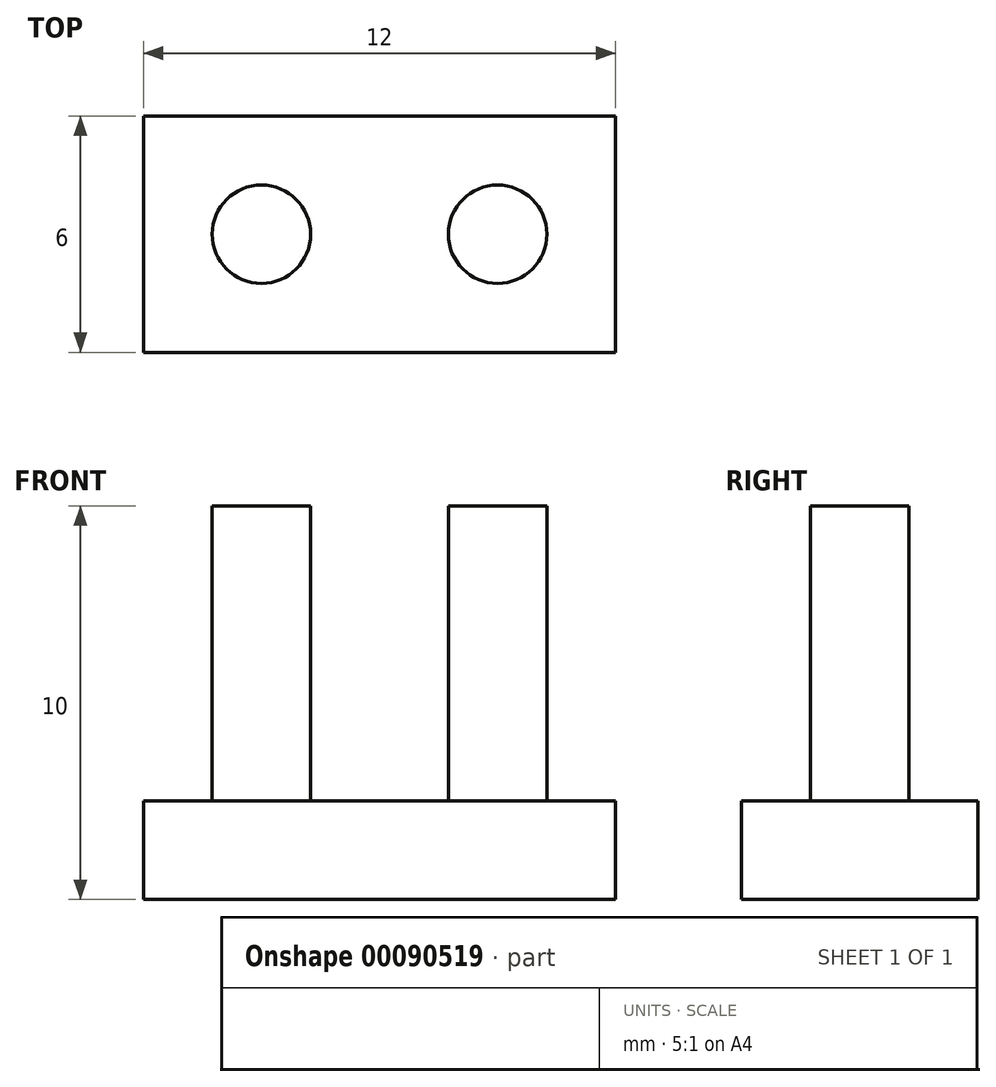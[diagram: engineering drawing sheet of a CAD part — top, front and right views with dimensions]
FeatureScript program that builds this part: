
annotation { "Feature Type Name" : "Feature", "Feature Type Description" : "" }
export const myFeature = defineFeature(function(context is Context, id is Id, definition is map)
    precondition{}
    {
        {
            var Q0;
            Q0=qCreatedBy(makeId("Top.planeOp"),FACE);
            var sketch = newSketch(context, id + "F0", { "sketchPlane" : qUnion([Q0])});
            skCircle(sketch, "E0", {"center": v(-3, 0) * mm, "radius": 2.5 * mm, "construction": true});
            skLineSegment(sketch, "E1", {"start": v(-3, 0) * mm, "end": v(0, 0) * mm, "construction": true});
            skLineSegment(sketch, "E2", {"start": v(-3, 0) * mm, "end": v(-6, 0) * mm, "construction": true});
            skLineSegment(sketch, "E3", {"start": v(-6, 0) * mm, "end": v(-9, 0) * mm, "construction": true});
            skLineSegment(sketch, "E4", {"start": v(-9, 0) * mm, "end": v(-12, 0) * mm, "construction": true});
            skCircle(sketch, "E5", {"center": v(-9, 0) * mm, "radius": 2.5 * mm, "construction": true});
            skCircle(sketch, "E6", {"center": v(-9, 0) * mm, "radius": 1.25 * mm});
            skCircle(sketch, "E7", {"center": v(-3, 0) * mm, "radius": 1.25 * mm});
            skLineSegment(sketch, "E8.bottom", {"start": v(0, 0) * mm, "end": v(-12, 0) * mm});
            skLineSegment(sketch, "E8.top", {"start": v(0, 3) * mm, "end": v(-12, 3) * mm});
            skLineSegment(sketch, "E8.left", {"start": v(0, 0) * mm, "end": v(0, 3) * mm});
            skLineSegment(sketch, "E8.right", {"start": v(-12, 0) * mm, "end": v(-12, 3) * mm});
            skLineSegment(sketch, "E9.top", {"start": v(0, -3) * mm, "end": v(-12, -3) * mm});
            skLineSegment(sketch, "E9.left", {"start": v(0, 0) * mm, "end": v(0, -3) * mm});
            skLineSegment(sketch, "E9.right", {"start": v(-12, 0) * mm, "end": v(-12, -3) * mm});
            skSolve(sketch);
        }
        {
            var Q0;
            Q0 = qSketchRegion(id + "F0", true);
            var Q1;
            {var subQ0=sQuery(id+"F0.wireOp",EDGE,"E8.bottom");var subQ1=sQuery(id+"F0.wireOp",EDGE,"E6");var subQ2=makeQuery(id+"F0.imprint","INTERSECT",VERTEX,{"disambiguationData":[OD(0.0)],"derivedFrom":[subQ1,subQ0]});Q1=makeQuery(id+"F0.imprint","IMPRINT",FACE,{"disambiguationData":[TD([[makeQuery(id+"F0.imprint","IMPRINT",EDGE,{"disambiguationData":[TD([[subQ2,1.0]])],"derivedFrom":subQ1}),1.0]])]});}
            var Q2;
            {var subQ0=sQuery(id+"F0.wireOp",EDGE,"E8.bottom");var subQ1=sQuery(id+"F0.wireOp",EDGE,"E6");var subQ2=makeQuery(id+"F0.imprint","INTERSECT",VERTEX,{"disambiguationData":[OD(0.0)],"derivedFrom":[subQ1,subQ0]});Q2=makeQuery(id+"F0.imprint","IMPRINT",FACE,{"disambiguationData":[TD([[makeQuery(id+"F0.imprint","IMPRINT",EDGE,{"disambiguationData":[TD([[subQ2,-1.0]])],"derivedFrom":subQ1}),1.0]])]});}
            var Q3;
            {var subQ0=sQuery(id+"F0.wireOp",EDGE,"E8.bottom");var subQ1=sQuery(id+"F0.wireOp",EDGE,"E7");var subQ2=makeQuery(id+"F0.imprint","INTERSECT",VERTEX,{"disambiguationData":[OD(0.0)],"derivedFrom":[subQ1,subQ0]});Q3=makeQuery(id+"F0.imprint","IMPRINT",FACE,{"disambiguationData":[TD([[makeQuery(id+"F0.imprint","IMPRINT",EDGE,{"disambiguationData":[TD([[subQ2,1.0]])],"derivedFrom":subQ1}),1.0]])]});}
            var Q4;
            {var subQ0=sQuery(id+"F0.wireOp",EDGE,"E8.bottom");var subQ1=sQuery(id+"F0.wireOp",EDGE,"E7");var subQ2=makeQuery(id+"F0.imprint","INTERSECT",VERTEX,{"disambiguationData":[OD(0.0)],"derivedFrom":[subQ1,subQ0]});Q4=makeQuery(id+"F0.imprint","IMPRINT",FACE,{"disambiguationData":[TD([[makeQuery(id+"F0.imprint","IMPRINT",EDGE,{"disambiguationData":[TD([[subQ2,-1.0]])],"derivedFrom":subQ1}),1.0]])]});}
            extrude(context, id + "F1", {"entities" : qUnion([Q0, Q1, Q2, Q3, Q4]), "oppositeDirection" : true, "depth" : 2.5 * mm});
        }
        {
            var Q0;
            {var subQ0=sQuery(id+"F0.wireOp",EDGE,"E8.bottom");var subQ1=sQuery(id+"F0.wireOp",EDGE,"E6");var subQ2=makeQuery(id+"F0.imprint","INTERSECT",VERTEX,{"disambiguationData":[OD(0.0)],"derivedFrom":[subQ1,subQ0]});Q0=makeQuery(id+"F0.imprint","IMPRINT",FACE,{"disambiguationData":[TD([[makeQuery(id+"F0.imprint","IMPRINT",EDGE,{"disambiguationData":[TD([[subQ2,-1.0]])],"derivedFrom":subQ1}),1.0]])]});}
            var Q1;
            {var subQ0=sQuery(id+"F0.wireOp",EDGE,"E8.bottom");var subQ1=sQuery(id+"F0.wireOp",EDGE,"E6");var subQ2=makeQuery(id+"F0.imprint","INTERSECT",VERTEX,{"disambiguationData":[OD(0.0)],"derivedFrom":[subQ1,subQ0]});Q1=makeQuery(id+"F0.imprint","IMPRINT",FACE,{"disambiguationData":[TD([[makeQuery(id+"F0.imprint","IMPRINT",EDGE,{"disambiguationData":[TD([[subQ2,1.0]])],"derivedFrom":subQ1}),1.0]])]});}
            var Q2;
            {var subQ0=sQuery(id+"F0.wireOp",EDGE,"E8.bottom");var subQ1=sQuery(id+"F0.wireOp",EDGE,"E7");var subQ2=makeQuery(id+"F0.imprint","INTERSECT",VERTEX,{"disambiguationData":[OD(0.0)],"derivedFrom":[subQ1,subQ0]});Q2=makeQuery(id+"F0.imprint","IMPRINT",FACE,{"disambiguationData":[TD([[makeQuery(id+"F0.imprint","IMPRINT",EDGE,{"disambiguationData":[TD([[subQ2,1.0]])],"derivedFrom":subQ1}),1.0]])]});}
            var Q3;
            {var subQ0=sQuery(id+"F0.wireOp",EDGE,"E8.bottom");var subQ1=sQuery(id+"F0.wireOp",EDGE,"E7");var subQ2=makeQuery(id+"F0.imprint","INTERSECT",VERTEX,{"disambiguationData":[OD(0.0)],"derivedFrom":[subQ1,subQ0]});Q3=makeQuery(id+"F0.imprint","IMPRINT",FACE,{"disambiguationData":[TD([[makeQuery(id+"F0.imprint","IMPRINT",EDGE,{"disambiguationData":[TD([[subQ2,-1.0]])],"derivedFrom":subQ1}),1.0]])]});}
            extrude(context, id + "F2", {"entities" : qUnion([Q0, Q1, Q2, Q3]), "operationType" : NewBodyOperationType.ADD, "depth" : 7.5 * mm});
        }
    });
